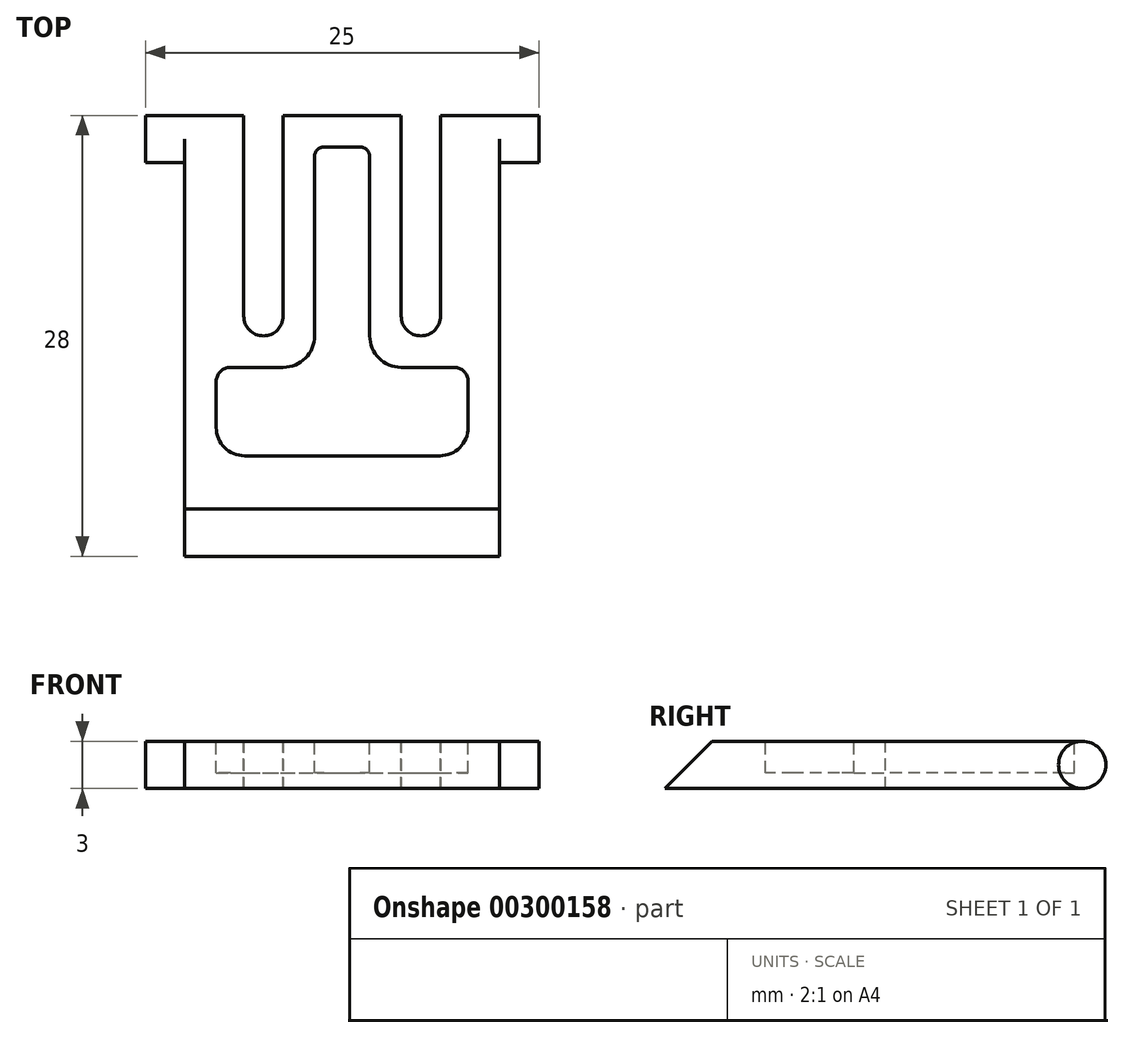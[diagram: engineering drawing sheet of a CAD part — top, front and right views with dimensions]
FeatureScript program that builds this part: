
annotation { "Feature Type Name" : "Feature", "Feature Type Description" : "" }
export const myFeature = defineFeature(function(context is Context, id is Id, definition is map)
    precondition{}
    {
        {
            var Q0;
            Q0=qCreatedBy(makeId("Top.planeOp"),FACE);
            var sketch = newSketch(context, id + "F0", { "sketchPlane" : qUnion([Q0])});
            skLineSegment(sketch, "E0.bottom", {"start": v(0, 0) * mm, "end": v(-20, 0) * mm});
            skLineSegment(sketch, "E0.top", {"start": v(0, -28) * mm, "end": v(-20, -28) * mm});
            skLineSegment(sketch, "E0.left", {"start": v(0, 0) * mm, "end": v(0, -28) * mm});
            skLineSegment(sketch, "E0.right", {"start": v(-20, 0) * mm, "end": v(-20, -28) * mm});
            skSolve(sketch);
        }
        {
            var Q0;
            Q0=makeQuery(id+"F0.imprint","IMPRINT",FACE,{"disambiguationData":[TD([[makeQuery(id+"F0.imprint","IMPRINT",EDGE,{"derivedFrom":sQuery(id+"F0.wireOp",EDGE,"E0.bottom")}),1.0]])]});
            extrude(context, id + "F1", {"entities" : qUnion([Q0]), "depth" : 3 * mm});
        }
        {
            var Q0;
            Q0=makeQuery(id+"F1.opExtrude","CAP_FACE",FACE,{"disambiguationData":[OSD([sQuery(id+"F0.wireOp",EDGE,"E0.bottom"),sQuery(id+"F0.wireOp",EDGE,"E0.top"),sQuery(id+"F0.wireOp",EDGE,"E0.left"),sQuery(id+"F0.wireOp",EDGE,"E0.right")])],"isStart":false});
            var sketch = newSketch(context, id + "F2", { "sketchPlane" : qUnion([Q0])});
            skLineSegment(sketch, "E1", {"start": v(-10, 0) * mm, "end": v(-10, -44.43) * mm, "construction": true});
            skLineSegment(sketch, "E2.bottom", {"start": v(-3.75, 0) * mm, "end": v(-6.25, 0) * mm});
            skLineSegment(sketch, "E2.top", {"start": v(-5, -14) * mm, "end": v(-5, -14) * mm});
            skLineSegment(sketch, "E2.left", {"start": v(-3.75, 0) * mm, "end": v(-3.75, -12.75) * mm});
            skLineSegment(sketch, "E2.right", {"start": v(-6.25, 0) * mm, "end": v(-6.25, -12.75) * mm});
            skLineSegment(sketch, "E3.MirrorCS", {"start": v(-13.75, 0) * mm, "end": v(-13.75, -12.75) * mm});
            skLineSegment(sketch, "E4.MirrorCS", {"start": v(-16.25, 0) * mm, "end": v(-16.25, -12.75) * mm});
            skLineSegment(sketch, "E5.MirrorCS", {"start": v(-16.25, 0) * mm, "end": v(-13.75, 0) * mm});
            skLineSegment(sketch, "E6.MirrorCS", {"start": v(-15, -14) * mm, "end": v(-15, -14) * mm});
            skPoint(sketch, "E7.visualSharp", {"position": v(-3.75, -14) * mm});
            skArc(sketch, "E7.filletArc", {"start": v(-5, -14) * mm, "mid": v(-4.12, -13.63) * mm, "end": v(-3.75, -12.75) * mm});
            skPoint(sketch, "E8.visualSharp", {"position": v(-6.25, -14) * mm});
            skArc(sketch, "E8.filletArc", {"start": v(-6.25, -12.75) * mm, "mid": v(-5.88, -13.63) * mm, "end": v(-5, -14) * mm});
            skPoint(sketch, "E9.visualSharp", {"position": v(-13.75, -14) * mm});
            skArc(sketch, "E9.filletArc", {"start": v(-15, -14) * mm, "mid": v(-14.12, -13.63) * mm, "end": v(-13.75, -12.75) * mm});
            skPoint(sketch, "E10.visualSharp", {"position": v(-16.25, -14) * mm});
            skArc(sketch, "E10.filletArc", {"start": v(-16.25, -12.75) * mm, "mid": v(-15.88, -13.63) * mm, "end": v(-15, -14) * mm});
            skSolve(sketch);
        }
        {
            var Q0;
            Q0=makeQuery(id+"F2.imprint","IMPRINT",FACE,{"disambiguationData":[TD([[makeQuery(id+"F2.imprint","IMPRINT",EDGE,{"derivedFrom":sQuery(id+"F2.wireOp",EDGE,"E3.MirrorCS")}),-1.0]])]});
            var Q1;
            Q1=makeQuery(id+"F2.imprint","IMPRINT",FACE,{"disambiguationData":[TD([[makeQuery(id+"F2.imprint","IMPRINT",EDGE,{"derivedFrom":sQuery(id+"F2.wireOp",EDGE,"E2.bottom")}),1.0]])]});
            extrude(context, id + "F3", {"entities" : qUnion([Q0, Q1]), "operationType" : NewBodyOperationType.REMOVE, "oppositeDirection" : true, "depth" : 25 * mm});
        }
        {
            var Q0;
            Q0=makeQuery(id+"F1.opExtrude","CAP_FACE",FACE,{"disambiguationData":[OSD([sQuery(id+"F0.wireOp",EDGE,"E0.bottom"),sQuery(id+"F0.wireOp",EDGE,"E0.top"),sQuery(id+"F0.wireOp",EDGE,"E0.left"),sQuery(id+"F0.wireOp",EDGE,"E0.right")])],"isStart":false});
            var sketch = newSketch(context, id + "F4", { "sketchPlane" : qUnion([Q0])});
            skLineSegment(sketch, "E11.bottom", {"start": v(-11.15, -2) * mm, "end": v(-8.85, -2) * mm});
            skLineSegment(sketch, "E11.left", {"start": v(-11.75, -2.6) * mm, "end": v(-11.75, -14) * mm});
            skLineSegment(sketch, "E11.right", {"start": v(-8.25, -2.6) * mm, "end": v(-8.25, -14) * mm});
            skLineSegment(sketch, "E12.bottom", {"start": v(-17.1, -16) * mm, "end": v(-13.75, -16) * mm});
            skLineSegment(sketch, "E12.top", {"start": v(-16.2, -21.62) * mm, "end": v(-3.8, -21.62) * mm});
            skLineSegment(sketch, "E12.left", {"start": v(-18, -16.9) * mm, "end": v(-18, -19.82) * mm});
            skLineSegment(sketch, "E12.right", {"start": v(-2, -16.9) * mm, "end": v(-2, -19.82) * mm});
            skLineSegment(sketch, "E13.trimOffspring", {"start": v(-6.25, -16) * mm, "end": v(-2.9, -16) * mm});
            skPoint(sketch, "E14.visualSharp", {"position": v(-11.75, -2) * mm});
            skArc(sketch, "E14.filletArc", {"start": v(-11.15, -2) * mm, "mid": v(-11.57, -2.18) * mm, "end": v(-11.75, -2.6) * mm});
            skPoint(sketch, "E15.visualSharp", {"position": v(-8.25, -2) * mm});
            skArc(sketch, "E15.filletArc", {"start": v(-8.25, -2.6) * mm, "mid": v(-8.43, -2.18) * mm, "end": v(-8.85, -2) * mm});
            skPoint(sketch, "E16.visualSharp", {"position": v(-8.25, -16) * mm});
            skArc(sketch, "E16.filletArc", {"start": v(-8.25, -14) * mm, "mid": v(-7.66, -15.41) * mm, "end": v(-6.25, -16) * mm});
            skPoint(sketch, "E17.visualSharp", {"position": v(-2, -21.62) * mm});
            skArc(sketch, "E17.filletArc", {"start": v(-3.8, -21.62) * mm, "mid": v(-2.53, -21.09) * mm, "end": v(-2, -19.82) * mm});
            skPoint(sketch, "E18.visualSharp", {"position": v(-18, -21.62) * mm});
            skArc(sketch, "E18.filletArc", {"start": v(-18, -19.82) * mm, "mid": v(-17.47, -21.09) * mm, "end": v(-16.2, -21.62) * mm});
            skPoint(sketch, "E19.visualSharp", {"position": v(-18, -16) * mm});
            skArc(sketch, "E19.filletArc", {"start": v(-17.1, -16) * mm, "mid": v(-17.74, -16.26) * mm, "end": v(-18, -16.9) * mm});
            skPoint(sketch, "E20.visualSharp", {"position": v(-11.75, -16) * mm});
            skArc(sketch, "E20.filletArc", {"start": v(-13.75, -16) * mm, "mid": v(-12.34, -15.41) * mm, "end": v(-11.75, -14) * mm});
            skPoint(sketch, "E21.visualSharp", {"position": v(-2, -16) * mm});
            skArc(sketch, "E21.filletArc", {"start": v(-2, -16.9) * mm, "mid": v(-2.26, -16.26) * mm, "end": v(-2.9, -16) * mm});
            skSolve(sketch);
        }
        {
            var Q0;
            Q0=makeQuery(id+"F4.imprint","IMPRINT",FACE,{"disambiguationData":[TD([[makeQuery(id+"F4.imprint","IMPRINT",EDGE,{"derivedFrom":sQuery(id+"F4.wireOp",EDGE,"E11.bottom")}),-1.0]])]});
            extrude(context, id + "F5", {"entities" : qUnion([Q0]), "operationType" : NewBodyOperationType.REMOVE, "oppositeDirection" : true, "depth" : 2 * mm});
        }
        {
            var Q0;
            Q0=makeQuery(id+"F1.opExtrude","SWEPT_FACE",FACE,{"disambiguationData":[OSD([sQuery(id+"F0.wireOp",EDGE,"E0.left")])]});
            var sketch = newSketch(context, id + "F6", { "sketchPlane" : qUnion([Q0])});
            skLineSegment(sketch, "E22", {"start": v(-28, 0) * mm, "end": v(-25, 3) * mm});
            skLineSegment(sketch, "E23", {"start": v(-25, 3) * mm, "end": v(-28, 3) * mm});
            skLineSegment(sketch, "E24", {"start": v(-28, 3) * mm, "end": v(-28, 0) * mm});
            skSolve(sketch);
        }
        {
            var Q0;
            Q0=makeQuery(id+"F6.imprint","IMPRINT",FACE,{"disambiguationData":[TD([[makeQuery(id+"F6.imprint","IMPRINT",EDGE,{"derivedFrom":sQuery(id+"F6.wireOp",EDGE,"E22")}),1.0]])]});
            extrude(context, id + "F7", {"entities" : qUnion([Q0]), "operationType" : NewBodyOperationType.REMOVE, "oppositeDirection" : true, "depth" : 32 * mm});
        }
        {
            var Q0;
            Q0=makeQuery(id+"F1.opExtrude","SWEPT_FACE",FACE,{"disambiguationData":[OSD([sQuery(id+"F0.wireOp",EDGE,"E0.left")])]});
            var sketch = newSketch(context, id + "F8", { "sketchPlane" : qUnion([Q0])});
            skCircle(sketch, "E25", {"center": v(-1.5, 1.5) * mm, "radius": 1.5 * mm});
            skSolve(sketch);
        }
        {
            var Q0;
            {var subQ0=sQuery(id+"F8.wireOp",EDGE,"E25");var subQ1=sQuery(id+"F0.wireOp",EDGE,"E0.left");var subQ2=makeQuery(id+"F8.imprint","INTERSECT",VERTEX,{"derivedFrom":[makeQuery(id+"F1.opExtrude","CAP_EDGE",EDGE,{"disambiguationData":[OSD([subQ1])],"isStart":false}),subQ0]});Q0=makeQuery(id+"F8.imprint","IMPRINT",FACE,{"disambiguationData":[TD([[makeQuery(id+"F8.imprint","IMPRINT",EDGE,{"disambiguationData":[TD([[subQ2,-1.0]])],"derivedFrom":subQ0}),1.0]])]});}
            extrude(context, id + "F9", {"entities" : qUnion([Q0]), "operationType" : NewBodyOperationType.ADD, "depth" : 2.5 * mm});
        }
        {
            var Q0;
            Q0=makeQuery(id+"F1.opExtrude","SWEPT_FACE",FACE,{"disambiguationData":[OSD([sQuery(id+"F0.wireOp",EDGE,"E0.right")])]});
            var sketch = newSketch(context, id + "F10", { "sketchPlane" : qUnion([Q0])});
            skCircle(sketch, "E26", {"center": v(1.5, 1.5) * mm, "radius": 1.5 * mm});
            skSolve(sketch);
        }
        {
            var Q0;
            Q0 = qSketchRegion(id + "F10", true);
            extrude(context, id + "F11", {"entities" : qUnion([Q0]), "operationType" : NewBodyOperationType.ADD, "depth" : 2.5 * mm});
        }
        {
            var Q0;
            {var subQ0=sQuery(id+"F0.wireOp",EDGE,"E0.bottom");var subQ1=sQuery(id+"F0.wireOp",EDGE,"E0.right");var subQ2=makeQuery(id+"F1.opExtrude","SWEPT_FACE",FACE,{"disambiguationData":[OSD([subQ1])]});Q0=makeQuery(id+"F11.boolean.opBoolean","SPLIT",FACE,{"disambiguationData":[TD([makeQuery(id+"F1.opExtrude","SWEPT_FACE",FACE,{"disambiguationData":[OSD([subQ0])]}),makeQuery(id+"F1.opExtrude","CAP_FACE",FACE,{"disambiguationData":[OSD([subQ0,sQuery(id+"F0.wireOp",EDGE,"E0.top"),sQuery(id+"F0.wireOp",EDGE,"E0.left"),subQ1])],"isStart":false}),subQ2,makeQuery(id+"F11.opExtrude","SWEPT_FACE",FACE,{"disambiguationData":[OSD([sQuery(id+"F10.wireOp",EDGE,"E26")])]})])],"derivedFrom":subQ2});}
            var Q1;
            {var subQ0=sQuery(id+"F0.wireOp",EDGE,"E0.bottom");var subQ1=sQuery(id+"F0.wireOp",EDGE,"E0.right");var subQ2=makeQuery(id+"F1.opExtrude","SWEPT_FACE",FACE,{"disambiguationData":[OSD([subQ1])]});Q1=makeQuery(id+"F11.boolean.opBoolean","SPLIT",FACE,{"disambiguationData":[TD([makeQuery(id+"F1.opExtrude","SWEPT_FACE",FACE,{"disambiguationData":[OSD([subQ0])]}),makeQuery(id+"F1.opExtrude","CAP_FACE",FACE,{"disambiguationData":[OSD([subQ0,sQuery(id+"F0.wireOp",EDGE,"E0.top"),sQuery(id+"F0.wireOp",EDGE,"E0.left"),subQ1])],"isStart":true}),subQ2,makeQuery(id+"F11.opExtrude","SWEPT_FACE",FACE,{"disambiguationData":[OSD([sQuery(id+"F10.wireOp",EDGE,"E26")])]})])],"derivedFrom":subQ2});}
            extrude(context, id + "F12", {"entities" : qUnion([Q0, Q1]), "operationType" : NewBodyOperationType.REMOVE, "oppositeDirection" : true, "depth" : 26.07 * mm});
        }
    });
